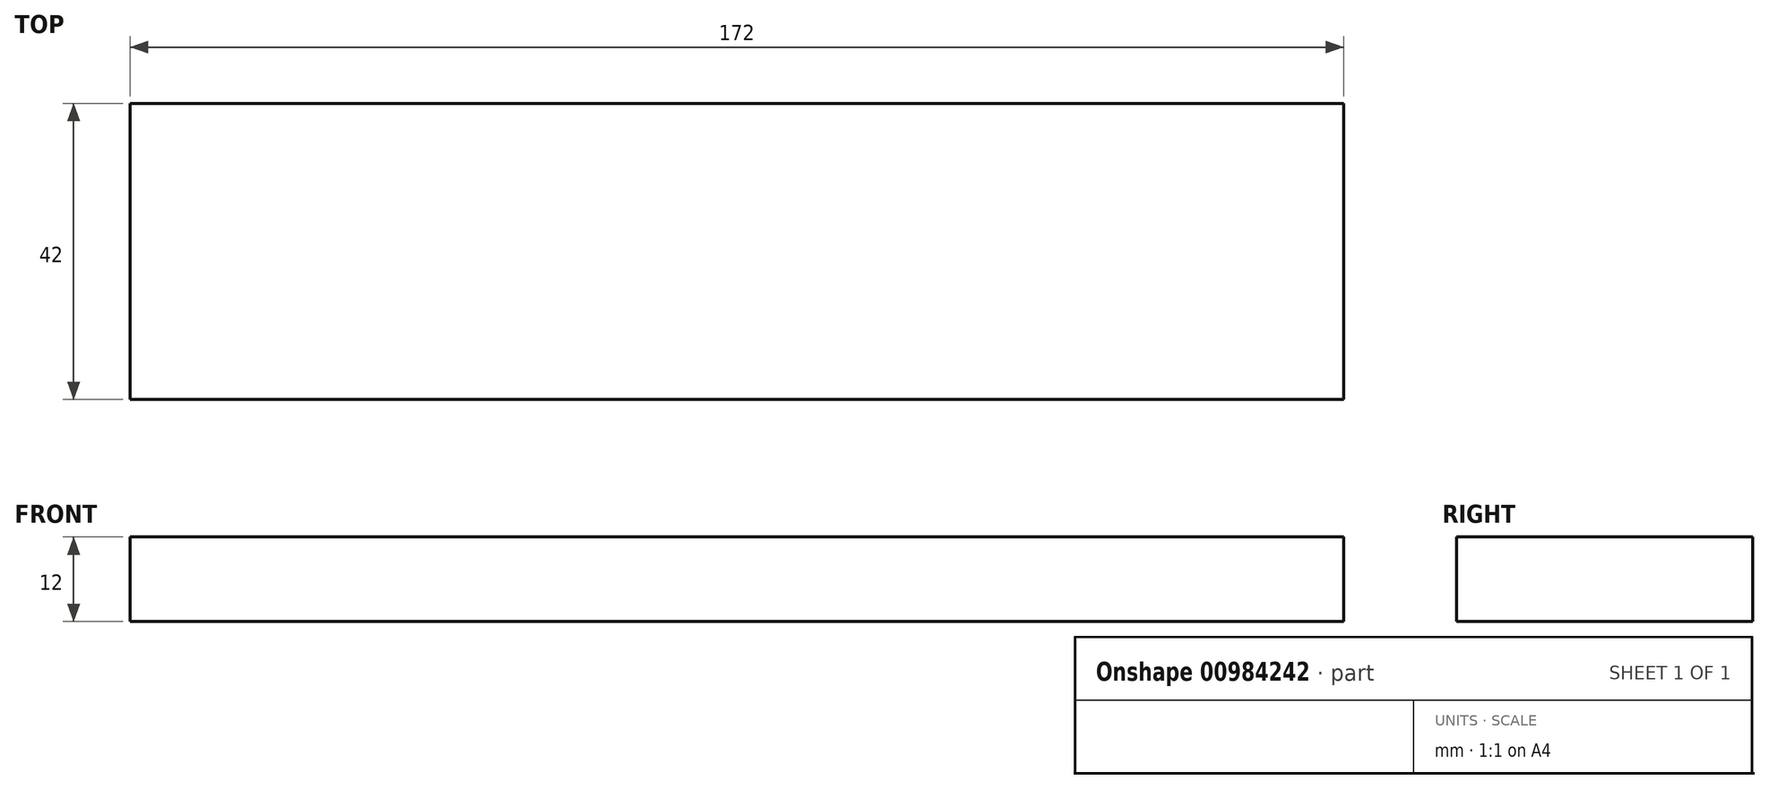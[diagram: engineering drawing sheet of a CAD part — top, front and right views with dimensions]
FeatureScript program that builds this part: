
annotation { "Feature Type Name" : "Feature", "Feature Type Description" : "" }
export const myFeature = defineFeature(function(context is Context, id is Id, definition is map)
    precondition{}
    {
        {
            var Q0;
            Q0=qCreatedBy(makeId("Top.planeOp"),FACE);
            var sketch = newSketch(context, id + "F0", { "sketchPlane" : qUnion([Q0])});
            skLineSegment(sketch, "E0.bottom", {"start": v(86, 21) * mm, "end": v(-86, 21) * mm});
            skLineSegment(sketch, "E0.top", {"start": v(86, -21) * mm, "end": v(-86, -21) * mm});
            skLineSegment(sketch, "E0.left", {"start": v(86, 21) * mm, "end": v(86, -21) * mm});
            skLineSegment(sketch, "E0.right", {"start": v(-86, 21) * mm, "end": v(-86, -21) * mm});
            skPoint(sketch, "E0.middle", {"position": v(0, 0) * mm});
            skSolve(sketch);
        }
        {
            var Q0;
            Q0=makeQuery(id+"F0.imprint","IMPRINT",FACE,{"disambiguationData":[TD([[makeQuery(id+"F0.imprint","IMPRINT",EDGE,{"derivedFrom":sQuery(id+"F0.wireOp",EDGE,"E0.bottom")}),1.0]])]});
            extrude(context, id + "F1", {"entities" : qUnion([Q0]), "oppositeDirection" : true, "depth" : 12 * mm, "offsetDistance" : 25 * mm});
        }
    });
